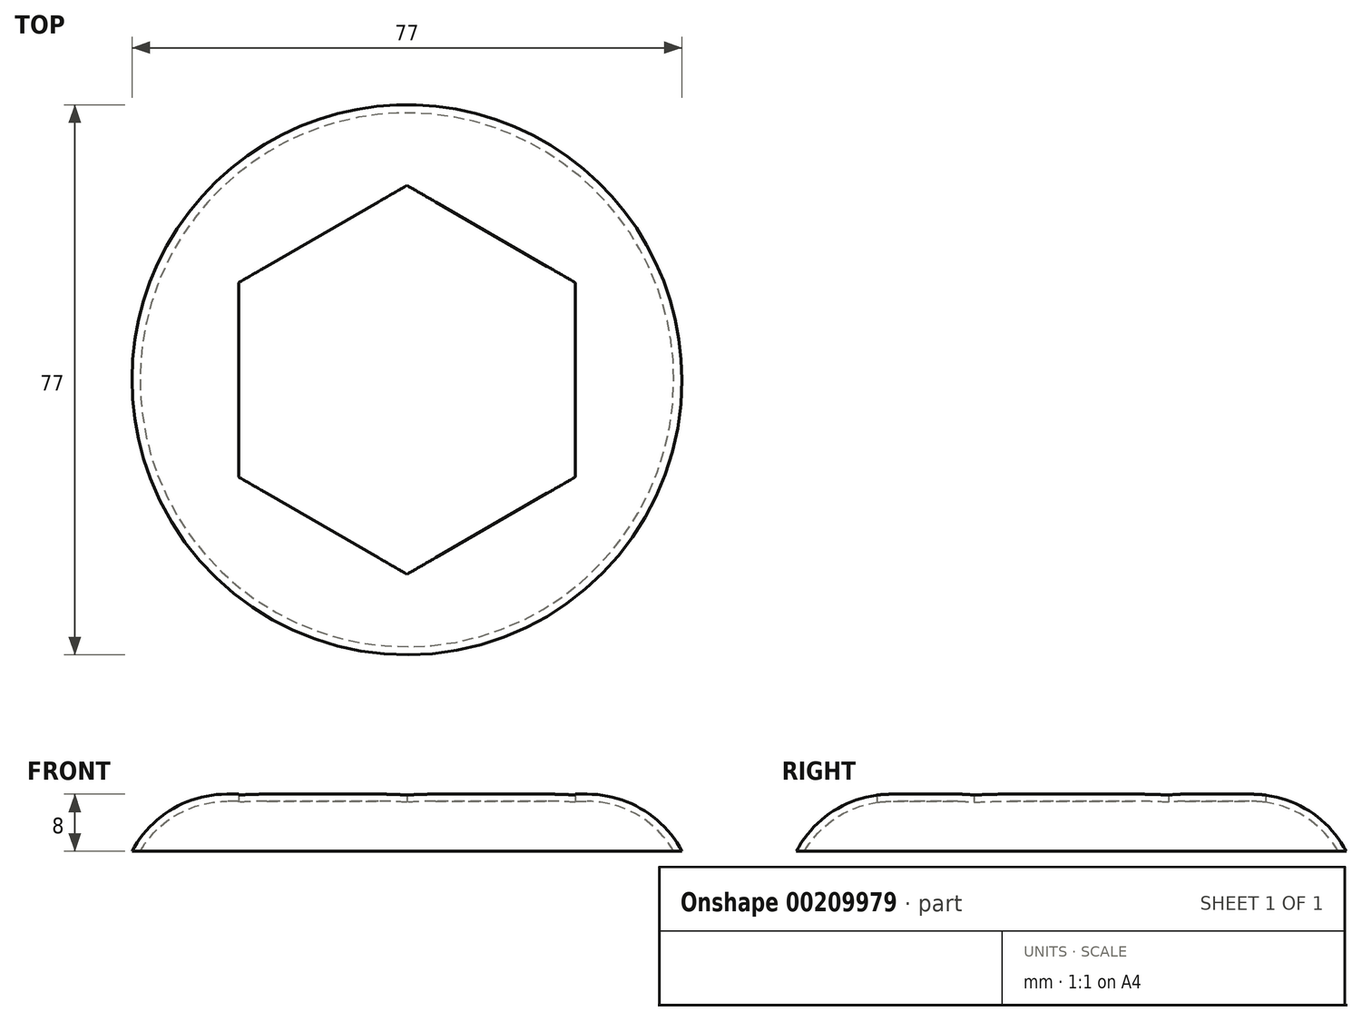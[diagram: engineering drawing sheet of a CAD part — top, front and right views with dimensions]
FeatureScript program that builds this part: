
annotation { "Feature Type Name" : "Feature", "Feature Type Description" : "" }
export const myFeature = defineFeature(function(context is Context, id is Id, definition is map)
    precondition{}
    {
        {
            var Q0;
            Q0=qCreatedBy(makeId("Top.planeOp"),FACE);
            var sketch = newSketch(context, id + "F0", { "sketchPlane" : qUnion([Q0])});
            skCircle(sketch, "E0", {"center": v(0, 0) * mm, "radius": 38.5 * mm});
            skSolve(sketch);
        }
        {
            var Q0;
            Q0=makeQuery(id+"F0.imprint","IMPRINT",FACE,{"disambiguationData":[TD([[makeQuery(id+"F0.imprint","IMPRINT",EDGE,{"derivedFrom":sQuery(id+"F0.wireOp",EDGE,"E0")}),1.0]])]});
            extrude(context, id + "F1", {"entities" : qUnion([Q0]), "depth" : 8 * mm});
        }
        {
            var Q0;
            Q0=makeQuery(id+"F1.opExtrude","CAP_FACE",FACE,{"disambiguationData":[OSD([sQuery(id+"F0.wireOp",EDGE,"E0")])],"isStart":false});
            var sketch = newSketch(context, id + "F2", { "sketchPlane" : qUnion([Q0])});
            skCircle(sketch, "E1.cCircle", {"center": v(0, 0) * mm, "radius": 22.5 * mm, "construction": true});
            skLineSegment(sketch, "E1.0", {"start": v(-22.53, 12.94) * mm, "end": v(-0.05, 25.98) * mm});
            skLineSegment(sketch, "E1.1", {"start": v(-0.05, 25.98) * mm, "end": v(22.47, 13.04) * mm});
            skLineSegment(sketch, "E1.2", {"start": v(22.47, 13.04) * mm, "end": v(22.53, -12.94) * mm});
            skLineSegment(sketch, "E1.3", {"start": v(22.53, -12.94) * mm, "end": v(0.05, -25.98) * mm});
            skLineSegment(sketch, "E1.4", {"start": v(0.05, -25.98) * mm, "end": v(-22.47, -13.04) * mm});
            skLineSegment(sketch, "E1.5", {"start": v(-22.47, -13.04) * mm, "end": v(-22.53, 12.94) * mm});
            skPoint(sketch, "E1.0.midPoint", {"position": v(-11.29, 19.46) * mm});
            skCircle(sketch, "E2", {"center": v(0, 0) * mm, "radius": 25 * mm, "construction": true});
            skSolve(sketch);
        }
        {
            var Q0;
            Q0=makeQuery(id+"F1.opExtrude","CAP_EDGE",EDGE,{"disambiguationData":[OSD([sQuery(id+"F0.wireOp",EDGE,"E0")])],"isStart":false});
            fillet(context, id + "F3", {"entities" : qUnion([Q0]), "radius" : 15 * mm, "tangentPropagation" : true, "allowEdgeOverflow" : false});
        }
        {
            var Q0;
            Q0=makeQuery(id+"F2.imprint","IMPRINT",FACE,{"disambiguationData":[TD([[makeQuery(id+"F2.imprint","IMPRINT",EDGE,{"derivedFrom":sQuery(id+"F2.wireOp",EDGE,"E1.0")}),-1.0]])]});
            extrude(context, id + "F4", {"entities" : qUnion([Q0]), "operationType" : NewBodyOperationType.REMOVE, "oppositeDirection" : true, "depth" : 8 * mm});
        }
        {
            var Q0;
            Q0=makeQuery(id+"F1.opExtrude","CAP_FACE",FACE,{"disambiguationData":[OSD([sQuery(id+"F0.wireOp",EDGE,"E0")])],"isStart":true});
            shell(context, id + "F5", {"entities" : qUnion([Q0]), "thickness" : 1 * mm});
        }
        {
            var Q0;
            Q0=qCreatedBy(makeId("Top.planeOp"),FACE);
            var sketch = newSketch(context, id + "F6", { "sketchPlane" : qUnion([Q0])});
            skCircle(sketch, "E3.cCircle", {"center": v(0, 0) * mm, "radius": 23.57 * mm, "construction": true});
            skLineSegment(sketch, "E3.0", {"start": v(-23.57, -13.6) * mm, "end": v(-23.57, 13.6) * mm});
            skLineSegment(sketch, "E3.1", {"start": v(-23.57, 13.6) * mm, "end": v(0, 27.22) * mm});
            skLineSegment(sketch, "E3.2", {"start": v(0, 27.22) * mm, "end": v(23.57, 13.6) * mm});
            skLineSegment(sketch, "E3.3", {"start": v(23.57, 13.6) * mm, "end": v(23.57, -13.6) * mm});
            skLineSegment(sketch, "E3.4", {"start": v(23.57, -13.6) * mm, "end": v(0, -27.22) * mm});
            skLineSegment(sketch, "E3.5", {"start": v(0, -27.22) * mm, "end": v(-23.57, -13.6) * mm});
            skPoint(sketch, "E3.0.midPoint", {"position": v(-23.57, 0) * mm});
            skSolve(sketch);
        }
        {
            var Q0;
            Q0 = qSketchRegion(id + "F6", true);
            extrude(context, id + "F7", {"entities" : qUnion([Q0]), "operationType" : NewBodyOperationType.REMOVE, "depth" : 25 * mm});
        }
    });
